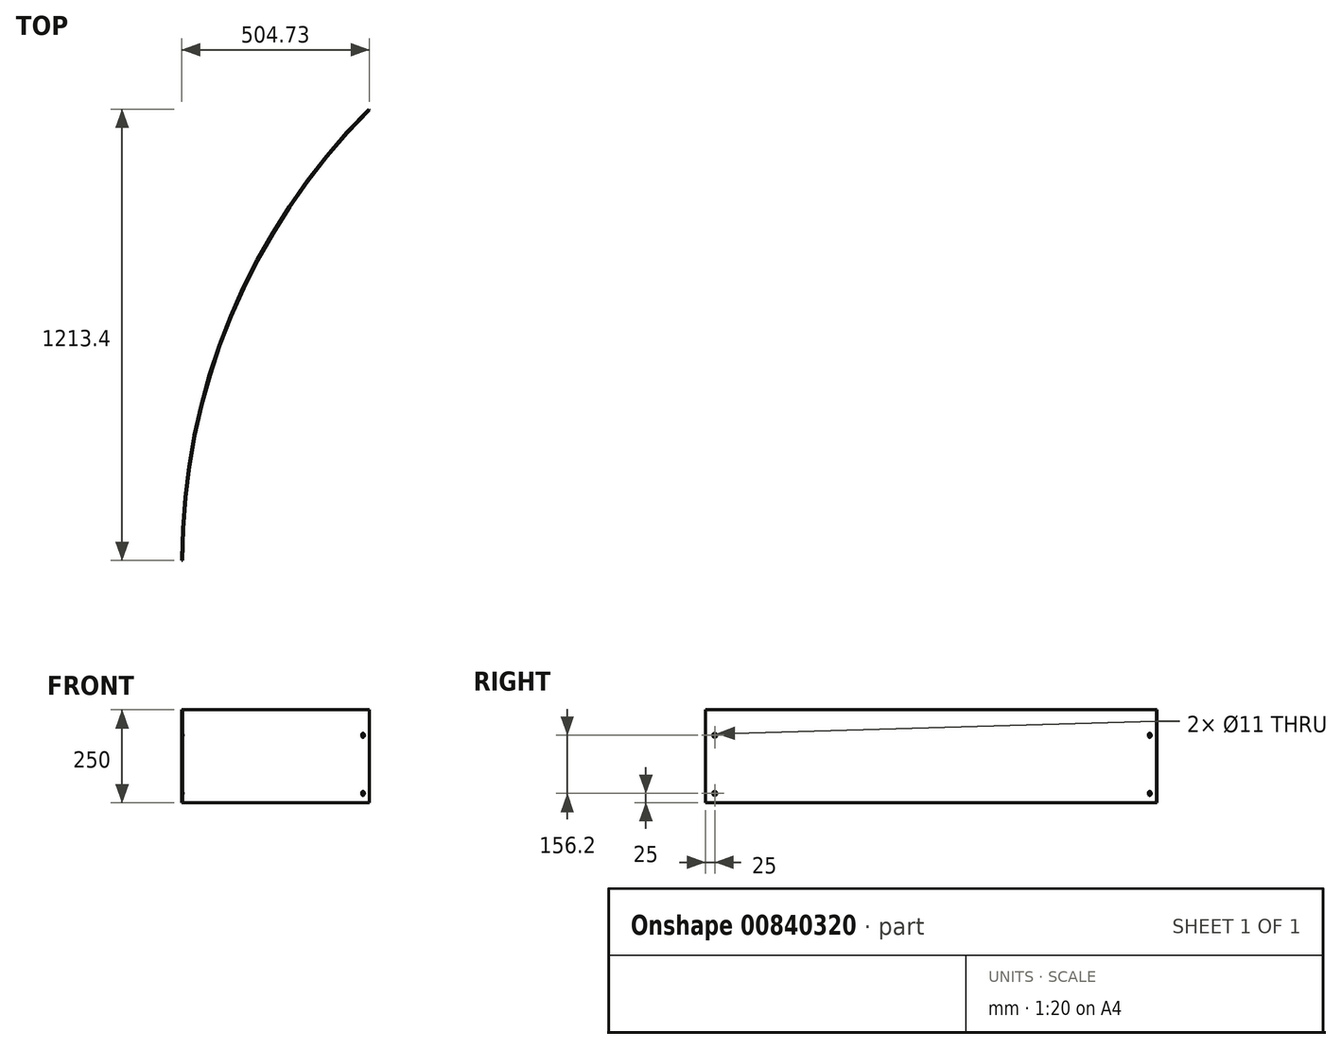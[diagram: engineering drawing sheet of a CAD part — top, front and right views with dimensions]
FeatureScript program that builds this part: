
annotation { "Feature Type Name" : "Feature", "Feature Type Description" : "" }
export const myFeature = defineFeature(function(context is Context, id is Id, definition is map)
    precondition{}
    {
        {
            var Q0;
            Q0=qCreatedBy(makeId("Top.planeOp"),FACE);
            var sketch = newSketch(context, id + "F0", { "sketchPlane" : qUnion([Q0])});
            skArc(sketch, "E0", {"start": v(501.73, 1211.27) * mm, "mid": v(130.4, 655.54) * mm, "end": v(0, 0) * mm});
            skLineSegment(sketch, "E1", {"start": v(0, 0) * mm, "end": v(1713, 0) * mm, "construction": true});
            skLineSegment(sketch, "E2", {"start": v(1713, 0) * mm, "end": v(501.73, 1211.27) * mm, "construction": true});
            skSolve(sketch);
        }
        {
            var Q0;
            Q0=qCreatedBy(makeId("Front.planeOp"),FACE);
            var sketch = newSketch(context, id + "F1", { "sketchPlane" : qUnion([Q0])});
            skLineSegment(sketch, "E3.bottom", {"start": v(0, 125) * mm, "end": v(-3, 125) * mm});
            skLineSegment(sketch, "E3.top", {"start": v(0, -125) * mm, "end": v(-3, -125) * mm});
            skLineSegment(sketch, "E3.left", {"start": v(0, 125) * mm, "end": v(0, -125) * mm});
            skLineSegment(sketch, "E3.right", {"start": v(-3, 125) * mm, "end": v(-3, -125) * mm});
            skSolve(sketch);
        }
        {
            var Q0;
            Q0=makeQuery(id+"F1.imprint","IMPRINT",FACE,{"disambiguationData":[TD([[makeQuery(id+"F1.imprint","IMPRINT",EDGE,{"derivedFrom":sQuery(id+"F1.wireOp",EDGE,"E3.bottom")}),1.0]])]});
            var Q1;
            Q1=sQuery(id+"F0.wireOp",EDGE,"A1xx75fL-8SPs-Z9ri-CPTb-JmtdQX2gj51n");
            var Q2;
            Q2=sQuery(id+"F0.wireOp",EDGE,"E0");
            var Q3;
            Q3=sQuery(id+"F0.wireOp",EDGE,"6DeDyjJt-B3l9-2hQ4-MW4A-s2AXSr22zXWG");
            sweep(context, id + "F2", {"profiles" : qUnion([Q0]), "path" : qUnion([Q1, Q2, Q3])});
        }
        {
            var Q0;
            Q0=qCreatedBy(makeId("Right.planeOp"),FACE);
            var sketch = newSketch(context, id + "F3", { "sketchPlane" : qUnion([Q0])});
            skPoint(sketch, "E4", {"position": v(25, -100) * mm});
            skPoint(sketch, "E5", {"position": v(25, 56.2) * mm});
            skCircle(sketch, "E6", {"center": v(25, 56.2) * mm, "radius": 5.5 * mm});
            skCircle(sketch, "E7", {"center": v(25, -100) * mm, "radius": 5.5 * mm});
            skSolve(sketch);
        }
        {
            var Q0;
            Q0=qSketchRegion(id+"F3",true);
            extrude(context, id + "F4", {"entities" : qUnion([Q0]), "operationType" : NewBodyOperationType.REMOVE, "endBound" : BoundingType.THROUGH_ALL, "depth" : 25 * mm, "offsetDistance" : 25 * mm, "hasSecondDirection" : true, "secondDirectionBound" : SecondDirectionBoundingType.THROUGH_ALL, "secondDirectionOppositeDirection" : true, "secondDirectionDepth" : 25 * mm});
        }
        {
            var Q0;
            Q0=qCreatedBy(makeId("Top.planeOp"),FACE);
            var sketch = newSketch(context, id + "F5", { "sketchPlane" : qUnion([Q0])});
            skLineSegment(sketch, "E8", {"start": v(0, 0) * mm, "end": v(353.55, 353.55) * mm, "construction": true});
            skSolve(sketch);
        }
        {
            var Q0;
            Q0=sQuery(id+"F5.wireOp",EDGE,"E8");
            var Q1;
            Q1=qCreatedBy(makeId("Right.planeOp"),FACE);
            cPlane(context, id + "F6", {"entities" : qUnion([Q0, Q1]), "cplaneType" : CPlaneType.LINE_ANGLE, "offset" : 25 * mm, "angle" : 0 * degree, "width" : 150 * mm, "height" : 150 * mm});
        }
        {
            var Q0;
            Q0=qCreatedBy(id+"F6.planeOp",FACE);
            var sketch = newSketch(context, id + "F7", { "sketchPlane" : qUnion([Q0])});
            skPoint(sketch, "E9", {"position": v(-1186.27, -100) * mm});
            skPoint(sketch, "E10", {"position": v(-1186.27, 56.2) * mm});
            skSolve(sketch);
        }
        {
            var Q0;
            Q0=sQuery(id+"F7.wireOp",VERTEX,"E10");
            var Q1;
            Q1=sQuery(id+"F7.wireOp",VERTEX,"E9");
            var Q2;
            Q2=makeQuery(id+"F2.opSweep","SWEPT_BODY",BODY,{"disambiguationData":[OSD([sQuery(id+"F0.wireOp",EDGE,"E0"),sQuery(id+"F1.wireOp",EDGE,"E3.bottom"),sQuery(id+"F1.wireOp",EDGE,"E3.top"),sQuery(id+"F1.wireOp",EDGE,"E3.left"),sQuery(id+"F1.wireOp",EDGE,"E3.right")])]});
            hole(context, id + "F8", {"style" : HoleStyle.SIMPLE, "endStyle" : HoleEndStyle.THROUGH, "oppositeDirection" : true, "standardTappedOrClearance" : lookupTablePath({ "fit" : "Normal", "standard" : "ISO", "size" : "M10", "type" : "Clearance" }), "standardBlindInLast" : lookupTablePath({ "fit" : "Standard", "standard" : "ISO", "size" : "M10", "type" : "Clearance" }), "holeDiameter" : 11 * mm, "majorDiameter" : 5 * mm, "isTappedThrough" : true, "tappedDepth" : 20 * mm, "tapClearance" : 3, "startFromSketch" : true, "locations" : qUnion([Q0, Q1]), "scope" : qUnion([Q2])});
        }
    });
